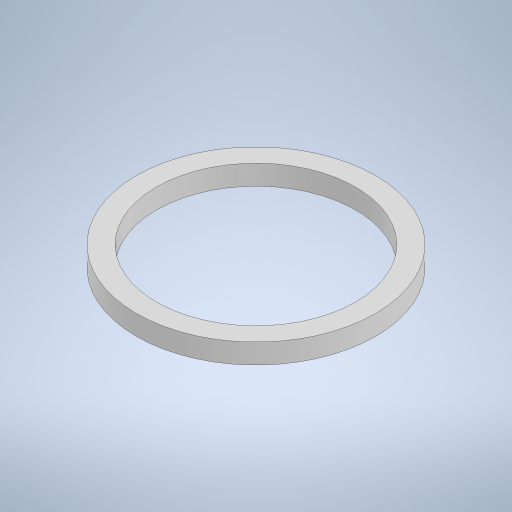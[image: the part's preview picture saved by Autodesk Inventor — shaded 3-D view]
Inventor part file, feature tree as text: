
AUTODESK INVENTOR PART (.ipt)
format: ipt  version: 2023 (Build 270158000, 158)  size: 231,936 bytes
history: native  units: mm
features: extrude x1, sketch x1
ambient origin geometry x8: Origin, YZ Plane, XZ Plane, XY Plane, X Axis, Y Axis, Z Axis, Center Point
bodies: Solid1 (feature_tree)
feature tree (2):
  extrude  "Extrusion1"  Depth=1.0mm
  sketch  "Sketch1"  dims[d0=10.0mm d1=12.0mm d2=1.0mm d3=0.0mm]
